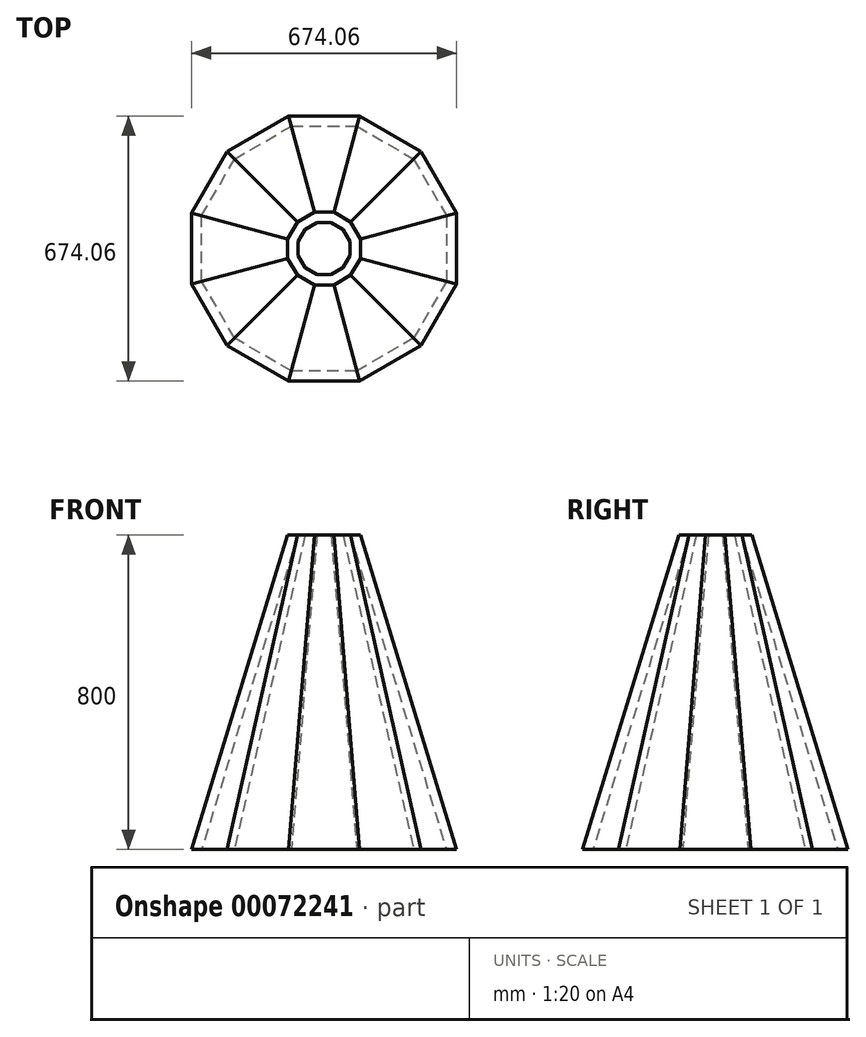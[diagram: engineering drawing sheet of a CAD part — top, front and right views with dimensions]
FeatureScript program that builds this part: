
annotation { "Feature Type Name" : "Feature", "Feature Type Description" : "" }
export const myFeature = defineFeature(function(context is Context, id is Id, definition is map)
    precondition{}
    {
        {
            var Q0;
            Q0=qCreatedBy(makeId("Top.planeOp"),FACE);
            var sketch = newSketch(context, id + "F0", { "sketchPlane" : qUnion([Q0])});
            skCircle(sketch, "E0.cCircle", {"center": v(0, 0) * mm, "radius": 335.88 * mm, "construction": true});
            skLineSegment(sketch, "E0.0", {"start": v(-90, 335.88) * mm, "end": v(90, 335.88) * mm});
            skLineSegment(sketch, "E0.1", {"start": v(90, 335.88) * mm, "end": v(245.88, 245.88) * mm});
            skLineSegment(sketch, "E0.2", {"start": v(245.88, 245.88) * mm, "end": v(335.88, 90) * mm});
            skLineSegment(sketch, "E0.3", {"start": v(335.88, 90) * mm, "end": v(335.88, -90) * mm});
            skLineSegment(sketch, "E0.4", {"start": v(335.88, -90) * mm, "end": v(245.88, -245.88) * mm});
            skLineSegment(sketch, "E0.5", {"start": v(245.88, -245.88) * mm, "end": v(90, -335.88) * mm});
            skLineSegment(sketch, "E0.6", {"start": v(90, -335.88) * mm, "end": v(-90, -335.88) * mm});
            skLineSegment(sketch, "E0.7", {"start": v(-90, -335.88) * mm, "end": v(-245.88, -245.88) * mm});
            skLineSegment(sketch, "E0.8", {"start": v(-245.88, -245.88) * mm, "end": v(-335.88, -90) * mm});
            skLineSegment(sketch, "E0.9", {"start": v(-335.88, -90) * mm, "end": v(-335.88, 90) * mm});
            skLineSegment(sketch, "E0.10", {"start": v(-335.88, 90) * mm, "end": v(-245.88, 245.88) * mm});
            skLineSegment(sketch, "E0.11", {"start": v(-245.88, 245.88) * mm, "end": v(-90, 335.88) * mm});
            skPoint(sketch, "E0.0.midPoint", {"position": v(0, 335.88) * mm});
            skLineSegment(sketch, "E1.0", {"start": v(-310.88, -83.3) * mm, "end": v(-310.88, 83.3) * mm});
            skLineSegment(sketch, "E1.1", {"start": v(227.58, 227.58) * mm, "end": v(310.88, 83.3) * mm});
            skLineSegment(sketch, "E1.2", {"start": v(83.3, 310.88) * mm, "end": v(227.58, 227.58) * mm});
            skLineSegment(sketch, "E1.3", {"start": v(-83.3, 310.88) * mm, "end": v(83.3, 310.88) * mm});
            skLineSegment(sketch, "E1.4", {"start": v(-227.58, 227.58) * mm, "end": v(-83.3, 310.88) * mm});
            skLineSegment(sketch, "E1.5", {"start": v(310.88, 83.3) * mm, "end": v(310.88, -83.3) * mm});
            skLineSegment(sketch, "E1.6", {"start": v(-310.88, 83.3) * mm, "end": v(-227.58, 227.58) * mm});
            skLineSegment(sketch, "E1.7", {"start": v(310.88, -83.3) * mm, "end": v(227.58, -227.58) * mm});
            skLineSegment(sketch, "E1.8", {"start": v(227.58, -227.58) * mm, "end": v(83.3, -310.88) * mm});
            skLineSegment(sketch, "E1.9", {"start": v(83.3, -310.88) * mm, "end": v(-83.3, -310.88) * mm});
            skLineSegment(sketch, "E1.10", {"start": v(-83.3, -310.88) * mm, "end": v(-227.58, -227.58) * mm});
            skLineSegment(sketch, "E1.11", {"start": v(-227.58, -227.58) * mm, "end": v(-310.88, -83.3) * mm});
            skSolve(sketch);
        }
        {
            var Q0;
            Q0=makeQuery(id+"F0.imprint","IMPRINT",FACE,{"disambiguationData":[TD([[makeQuery(id+"F0.imprint","IMPRINT",EDGE,{"derivedFrom":sQuery(id+"F0.wireOp",EDGE,"E1.0")}),-1.0]])]});
            cPlane(context, id + "F1", {"entities" : qUnion([Q0]), "cplaneType" : CPlaneType.OFFSET, "offset" : 800 * mm, "width" : 150 * mm, "height" : 150 * mm});
        }
        {
            var Q0;
            Q0=makeQuery(id+"F0.imprint","IMPRINT",FACE,{"disambiguationData":[TD([[makeQuery(id+"F0.imprint","IMPRINT",EDGE,{"derivedFrom":sQuery(id+"F0.wireOp",EDGE,"E1.0")}),-1.0]])]});
            extrude(context, id + "F2", {"entities" : qUnion([Q0]), "depth" : 800 * mm, "hasDraft" : true, "draftAngle" : 17 * degree, "draftPullDirection" : true});
        }
        {
            var Q0;
            Q0=makeQuery(id+"F2.opExtrude","CAP_FACE",FACE,{"disambiguationData":[OSD([sQuery(id+"F0.wireOp",EDGE,"E1.0"),sQuery(id+"F0.wireOp",EDGE,"E1.1"),sQuery(id+"F0.wireOp",EDGE,"E1.2"),sQuery(id+"F0.wireOp",EDGE,"E1.3"),sQuery(id+"F0.wireOp",EDGE,"E1.4"),sQuery(id+"F0.wireOp",EDGE,"E1.5"),sQuery(id+"F0.wireOp",EDGE,"E1.6"),sQuery(id+"F0.wireOp",EDGE,"E1.7"),sQuery(id+"F0.wireOp",EDGE,"E1.8"),sQuery(id+"F0.wireOp",EDGE,"E1.9"),sQuery(id+"F0.wireOp",EDGE,"E1.10"),sQuery(id+"F0.wireOp",EDGE,"E1.11")])],"isStart":true});
            shell(context, id + "F3", {"entities" : qUnion([Q0]), "thickness" : 25 * mm, "oppositeDirection" : true});
        }
        {
            var Q0;
            Q0=qCreatedBy(id+"F1.planeOp",FACE);
            var sketch = newSketch(context, id + "F4", { "sketchPlane" : qUnion([Q0])});
            skCircle(sketch, "E2.cCircle", {"center": v(0, 0) * mm, "radius": 93.3 * mm, "construction": true});
            skLineSegment(sketch, "E2.0", {"start": v(93.3, 25) * mm, "end": v(93.3, -25) * mm});
            skLineSegment(sketch, "E2.1", {"start": v(93.3, -25) * mm, "end": v(68.3, -68.3) * mm});
            skLineSegment(sketch, "E2.2", {"start": v(68.3, -68.3) * mm, "end": v(25, -93.3) * mm});
            skLineSegment(sketch, "E2.3", {"start": v(25, -93.3) * mm, "end": v(-25, -93.3) * mm});
            skLineSegment(sketch, "E2.4", {"start": v(-25, -93.3) * mm, "end": v(-68.3, -68.3) * mm});
            skLineSegment(sketch, "E2.5", {"start": v(-68.3, -68.3) * mm, "end": v(-93.3, -25) * mm});
            skLineSegment(sketch, "E2.6", {"start": v(-93.3, -25) * mm, "end": v(-93.3, 25) * mm});
            skLineSegment(sketch, "E2.7", {"start": v(-93.3, 25) * mm, "end": v(-68.3, 68.3) * mm});
            skLineSegment(sketch, "E2.8", {"start": v(-68.3, 68.3) * mm, "end": v(-25, 93.3) * mm});
            skLineSegment(sketch, "E2.9", {"start": v(-25, 93.3) * mm, "end": v(25, 93.3) * mm});
            skLineSegment(sketch, "E2.10", {"start": v(25, 93.3) * mm, "end": v(68.3, 68.3) * mm});
            skLineSegment(sketch, "E2.11", {"start": v(68.3, 68.3) * mm, "end": v(93.3, 25) * mm});
            skPoint(sketch, "E2.0.midPoint", {"position": v(93.3, 0) * mm});
            skSolve(sketch);
        }
        {
            var Q0;
            Q0 = qSketchRegion(id + "F4", true);
            extrude(context, id + "F5", {"entities" : qUnion([Q0]), "operationType" : NewBodyOperationType.REMOVE, "depth" : 25 * mm});
        }
    });
